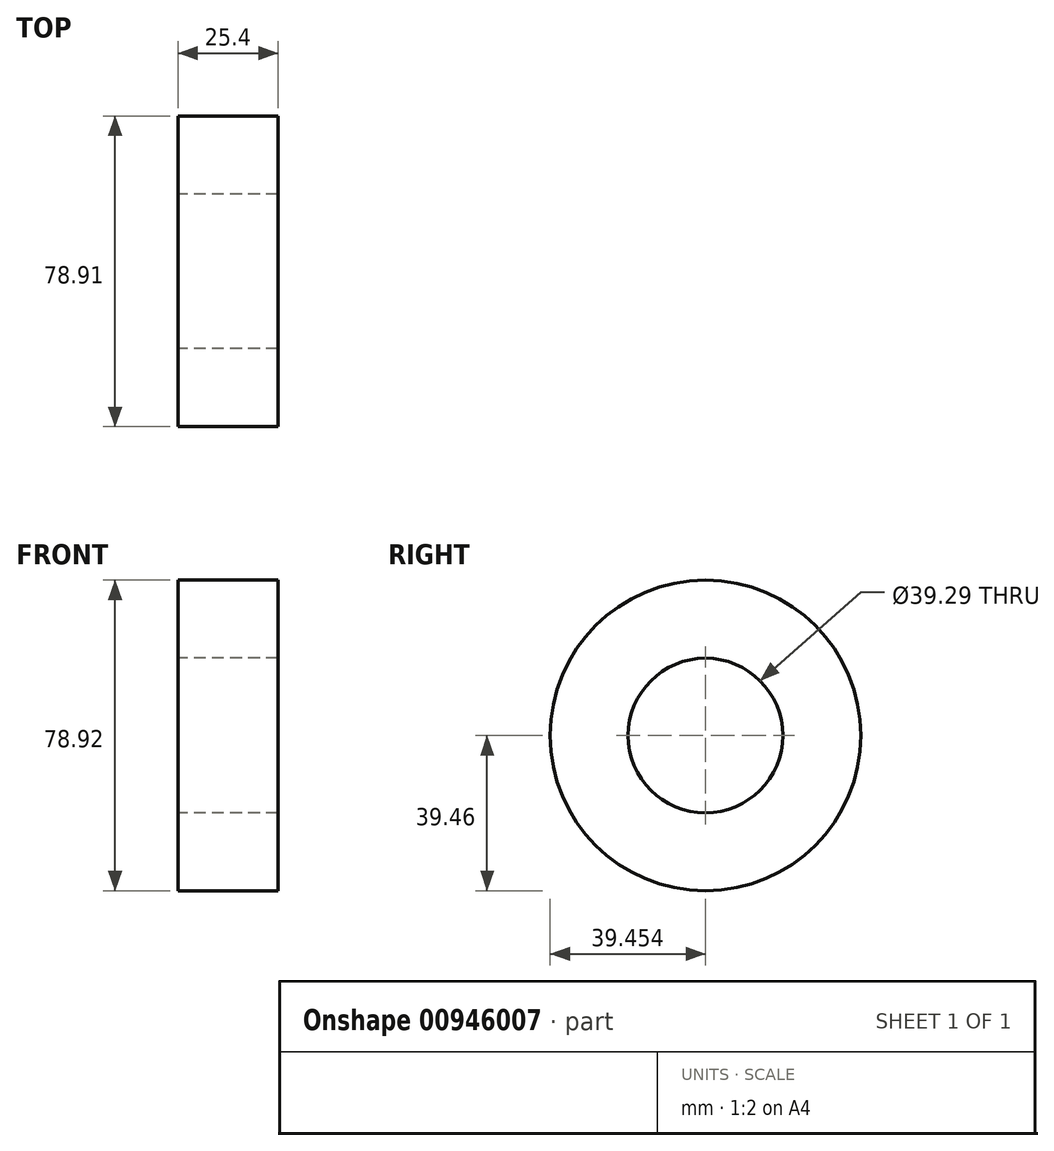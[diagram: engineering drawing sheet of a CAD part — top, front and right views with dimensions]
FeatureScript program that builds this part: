
annotation { "Feature Type Name" : "Feature", "Feature Type Description" : "" }
export const myFeature = defineFeature(function(context is Context, id is Id, definition is map)
    precondition{}
    {
        {
            var Q0;
            Q0=qCreatedBy(makeId("Right.planeOp"),FACE);
            var sketch = newSketch(context, id + "F0", { "sketchPlane" : qUnion([Q0])});
            skCircle(sketch, "E0", {"center": v(-7.09, 0) * mm, "radius": 39.46 * mm});
            skCircle(sketch, "E1", {"center": v(-7.09, 0) * mm, "radius": 19.65 * mm});
            skSolve(sketch);
        }
        {
            var Q0;
            Q0=makeQuery(id+"F0.imprint","IMPRINT",FACE,{"disambiguationData":[TD([[makeQuery(id+"F0.imprint","IMPRINT",EDGE,{"derivedFrom":sQuery(id+"F0.wireOp",EDGE,"E0")}),1.0]])]});
            extrude(context, id + "F1", {"entities" : qUnion([Q0]), "depth" : 25.4 * mm, "offsetDistance" : 25.4 * mm});
        }
    });
